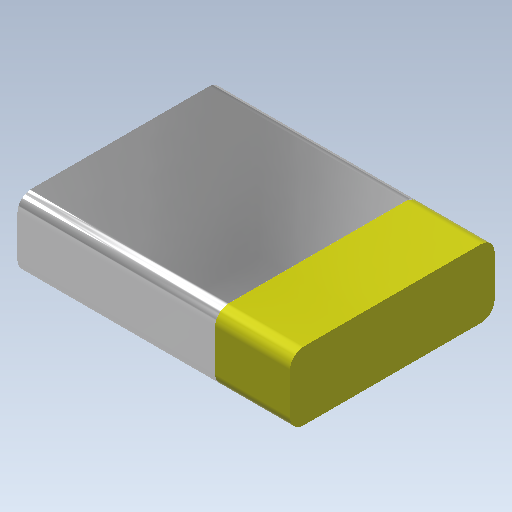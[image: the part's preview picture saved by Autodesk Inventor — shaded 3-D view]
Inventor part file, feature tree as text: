
AUTODESK INVENTOR PART (.ipt)
format: ipt  version: 2020 (Build 240168000, 168)  size: 136,192 bytes
history: native  units: mm
features: other x3, extrude x1, plane x1, split x1, fillet x1, sketch x1
ambient origin geometry x8: Origin, YZ Plane, XZ Plane, XY Plane, X Axis, Y Axis, Z Axis, Center Point
bodies: Body1 (feature_tree), Body2 (feature_tree)
feature tree (8):
  other  "Sólido1"
  extrude  "Extrusión1"  Depth=15.0mm
  plane  "Plano de trabajo1"
  split  "Dividir1"
  fillet  "Empalme1"  Radius=5.0mm
  sketch  "Boceto1"  dims[d0=20.0mm d1=15.0mm d2=5.0mm d3=0.0mm d4=-5.5mm d5=1.0mm]
  other  "Sólido2"
  other  "Sólido3"
